# Revit family: NLRS_33_RB_DO_BILCO_dakluik_J-AL
name_source: partatom
category: Doors
revit_build: Autodesk Revit 2015 (Build: 20140223_1515(x64)
units: mm (PartAtom-declared; Revit-internal decimal feet)

## types (1)
- NLRS_33_RB_DO_BILCO_dakluik_J-AL
    Description = standaard vloerluik
    LiftingMechanismHeight = 292 mm  [stored 0.958005 ft]
    Manufacturer = Bilco
    Model = J1AL
    bediening = handmatig
    belasting = 1464.00 kg/m²
    brandwerend 60 min = No
    breedte = 1217 mm  [stored 3.99278 ft]
    cilinderslot = Yes
    code productgroep = LUI
    conservering = brut
    dagmaatbreedte = 1065 mm  [stored 3.49409 ft]
    dagmaatlengte = 1065 mm  [stored 3.49409 ft]
    deurblad = tranenplaat
    false = No
    gewicht (kg) = 61
    hoogte_opstand = 89 mm  [stored 0.291995 ft]
    lengte = 1217 mm  [stored 3.99278 ft]
    loopslot = Yes
    materiaal = bcb_aluminium
    omranding blokkozijn = No
    omranding dakopstand = No
    omranding hoekprofiel = No
    omranding waterafvoerend = Yes
    omschrijving = standaard vloerluik
    openingshoek = 90.00°
    openstand vergrendeling = Yes
    plaatdikte = 6 mm  [stored 0.019685 ft]
    productgroep = Dakluiken
    scharnierend = Yes
    true = Yes
    vaste ladder = Yes
    veersysteem = Yes
    veiligheidsrailing = Yes
    vuilafdichting = Yes

note: [stored X ft] marks values corroborated as IEEE doubles in the binary element streams (Revit-internal decimal feet)

## geometry (parser evidence)
native form markers: Blend x4, Sweep x9
no freeform markers — native parametric forms only
